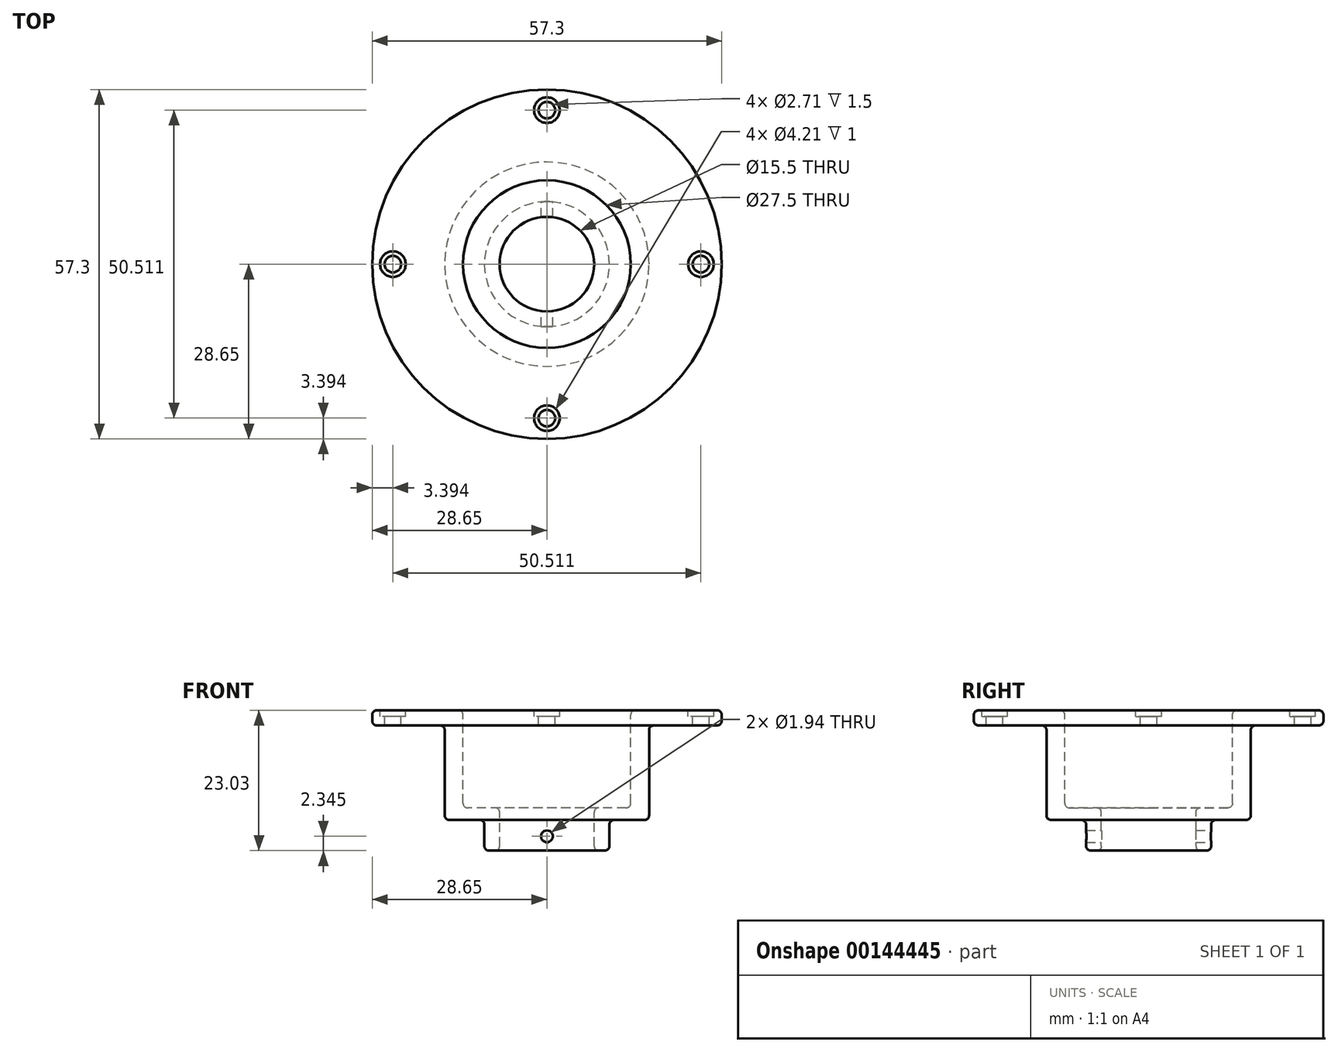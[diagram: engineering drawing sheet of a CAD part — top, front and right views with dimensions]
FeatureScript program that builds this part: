
annotation { "Feature Type Name" : "Feature", "Feature Type Description" : "" }
export const myFeature = defineFeature(function(context is Context, id is Id, definition is map)
    precondition{}
    {
        {
            var Q0;
            Q0=qCreatedBy(makeId("Front.planeOp"),FACE);
            var sketch = newSketch(context, id + "F0", { "sketchPlane" : qUnion([Q0])});
            skLineSegment(sketch, "E0", {"start": v(0, 0) * mm, "end": v(7.75, 0) * mm});
            skLineSegment(sketch, "E1", {"start": v(7.75, 0) * mm, "end": v(7.75, 7.03) * mm});
            skLineSegment(sketch, "E2", {"start": v(7.75, 7.03) * mm, "end": v(13.75, 7.03) * mm});
            skLineSegment(sketch, "E3", {"start": v(13.75, 7.03) * mm, "end": v(13.75, 23.03) * mm});
            skLineSegment(sketch, "E4", {"start": v(13.75, 23.03) * mm, "end": v(28.65, 23.03) * mm});
            skLineSegment(sketch, "E5", {"start": v(28.65, 23.03) * mm, "end": v(28.65, 20.53) * mm});
            skLineSegment(sketch, "E6", {"start": v(28.65, 20.53) * mm, "end": v(16.75, 20.53) * mm});
            skLineSegment(sketch, "E7", {"start": v(16.75, 20.53) * mm, "end": v(16.75, 5.03) * mm});
            skLineSegment(sketch, "E8", {"start": v(16.75, 5.03) * mm, "end": v(10.25, 5.03) * mm});
            skLineSegment(sketch, "E9", {"start": v(10.25, 5.03) * mm, "end": v(10.25, 0) * mm});
            skLineSegment(sketch, "E10", {"start": v(10.25, 0) * mm, "end": v(7.75, 0) * mm});
            skLineSegment(sketch, "E11", {"start": v(0, 26.24) * mm, "end": v(0, -4.42) * mm});
            skSolve(sketch);
        }
        {
            var Q0;
            Q0 = qSketchRegion(id + "F0", true);
            var Q1;
            Q1=sQuery(id+"F0.wireOp",EDGE,"E11");
            revolve(context, id + "F1", {"entities" : qUnion([Q0]), "axis" : qUnion([Q1]), "revolveType" : RevolveType.FULL});
        }
        {
            var Q0;
            Q0=makeQuery(id+"F1.opRevolve","SWEPT_FACE",FACE,{"disambiguationData":[OSD([sQuery(id+"F0.wireOp",EDGE,"E4")])]});
            var sketch = newSketch(context, id + "F2", { "sketchPlane" : qUnion([Q0])});
            skCircle(sketch, "E12", {"center": v(0, 0) * mm, "radius": 25.26 * mm});
            skCircle(sketch, "E13", {"center": v(25.26, 0) * mm, "radius": 1.35 * mm});
            skCircle(sketch, "E14", {"center": v(0, 0) * mm, "radius": 26.6 * mm});
            skCircle(sketch, "E15", {"center": v(0, 25.26) * mm, "radius": 1.35 * mm});
            skCircle(sketch, "E16", {"center": v(-25.26, 0) * mm, "radius": 1.35 * mm});
            skCircle(sketch, "E17", {"center": v(0, -25.26) * mm, "radius": 1.35 * mm});
            skSolve(sketch);
        }
        {
            var Q0;
            {var subQ0=sQuery(id+"F2.wireOp",EDGE,"E17");var subQ1=sQuery(id+"F2.wireOp",EDGE,"E12");var subQ2=makeQuery(id+"F2.imprint","INTERSECT",VERTEX,{"disambiguationData":[OD(0.0)],"derivedFrom":[subQ1,subQ0]});Q0=makeQuery(id+"F2.imprint","IMPRINT",FACE,{"disambiguationData":[TD([[makeQuery(id+"F2.imprint","IMPRINT",EDGE,{"disambiguationData":[TD([[subQ2,-1.0]])],"derivedFrom":subQ1}),-1.0]])]});}
            var Q1;
            {var subQ0=sQuery(id+"F2.wireOp",EDGE,"E17");var subQ1=sQuery(id+"F2.wireOp",EDGE,"E12");var subQ2=makeQuery(id+"F2.imprint","INTERSECT",VERTEX,{"disambiguationData":[OD(0.0)],"derivedFrom":[subQ1,subQ0]});Q1=makeQuery(id+"F2.imprint","IMPRINT",FACE,{"disambiguationData":[TD([[makeQuery(id+"F2.imprint","IMPRINT",EDGE,{"disambiguationData":[TD([[subQ2,-1.0]])],"derivedFrom":subQ1}),1.0]])]});}
            var Q2;
            {var subQ0=sQuery(id+"F2.wireOp",EDGE,"E13");var subQ1=sQuery(id+"F2.wireOp",EDGE,"E12");var subQ2=makeQuery(id+"F2.imprint","INTERSECT",VERTEX,{"disambiguationData":[OD(0.0)],"derivedFrom":[subQ1,subQ0]});Q2=makeQuery(id+"F2.imprint","IMPRINT",FACE,{"disambiguationData":[TD([[makeQuery(id+"F2.imprint","IMPRINT",EDGE,{"disambiguationData":[TD([[subQ2,1.0]])],"derivedFrom":subQ1}),-1.0]])]});}
            var Q3;
            {var subQ0=sQuery(id+"F2.wireOp",EDGE,"E13");var subQ1=sQuery(id+"F2.wireOp",EDGE,"E12");var subQ2=makeQuery(id+"F2.imprint","INTERSECT",VERTEX,{"disambiguationData":[OD(0.0)],"derivedFrom":[subQ1,subQ0]});Q3=makeQuery(id+"F2.imprint","IMPRINT",FACE,{"disambiguationData":[TD([[makeQuery(id+"F2.imprint","IMPRINT",EDGE,{"disambiguationData":[TD([[subQ2,1.0]])],"derivedFrom":subQ1}),1.0]])]});}
            var Q4;
            {var subQ0=sQuery(id+"F2.wireOp",EDGE,"E15");var subQ1=sQuery(id+"F2.wireOp",EDGE,"E12");var subQ2=makeQuery(id+"F2.imprint","INTERSECT",VERTEX,{"disambiguationData":[OD(0.0)],"derivedFrom":[subQ1,subQ0]});Q4=makeQuery(id+"F2.imprint","IMPRINT",FACE,{"disambiguationData":[TD([[makeQuery(id+"F2.imprint","IMPRINT",EDGE,{"disambiguationData":[TD([[subQ2,-1.0]])],"derivedFrom":subQ1}),-1.0]])]});}
            var Q5;
            {var subQ0=sQuery(id+"F2.wireOp",EDGE,"E15");var subQ1=sQuery(id+"F2.wireOp",EDGE,"E12");var subQ2=makeQuery(id+"F2.imprint","INTERSECT",VERTEX,{"disambiguationData":[OD(0.0)],"derivedFrom":[subQ1,subQ0]});Q5=makeQuery(id+"F2.imprint","IMPRINT",FACE,{"disambiguationData":[TD([[makeQuery(id+"F2.imprint","IMPRINT",EDGE,{"disambiguationData":[TD([[subQ2,-1.0]])],"derivedFrom":subQ1}),1.0]])]});}
            var Q6;
            {var subQ0=sQuery(id+"F2.wireOp",EDGE,"E16");var subQ1=sQuery(id+"F2.wireOp",EDGE,"E12");var subQ2=makeQuery(id+"F2.imprint","INTERSECT",VERTEX,{"disambiguationData":[OD(0.0)],"derivedFrom":[subQ1,subQ0]});Q6=makeQuery(id+"F2.imprint","IMPRINT",FACE,{"disambiguationData":[TD([[makeQuery(id+"F2.imprint","IMPRINT",EDGE,{"disambiguationData":[TD([[subQ2,-1.0]])],"derivedFrom":subQ1}),-1.0]])]});}
            var Q7;
            {var subQ0=sQuery(id+"F2.wireOp",EDGE,"E16");var subQ1=sQuery(id+"F2.wireOp",EDGE,"E12");var subQ2=makeQuery(id+"F2.imprint","INTERSECT",VERTEX,{"disambiguationData":[OD(0.0)],"derivedFrom":[subQ1,subQ0]});Q7=makeQuery(id+"F2.imprint","IMPRINT",FACE,{"disambiguationData":[TD([[makeQuery(id+"F2.imprint","IMPRINT",EDGE,{"disambiguationData":[TD([[subQ2,-1.0]])],"derivedFrom":subQ1}),1.0]])]});}
            extrude(context, id + "F3", {"entities" : qUnion([Q0, Q1, Q2, Q3, Q4, Q5, Q6, Q7]), "operationType" : NewBodyOperationType.REMOVE, "oppositeDirection" : true, "depth" : 25 * mm});
        }
        {
            var Q0;
            Q0=makeQuery(id+"F1.opRevolve","SWEPT_FACE",FACE,{"disambiguationData":[OSD([sQuery(id+"F0.wireOp",EDGE,"E4")])]});
            var sketch = newSketch(context, id + "F4", { "sketchPlane" : qUnion([Q0])});
            skCircle(sketch, "E18", {"center": v(0, 0) * mm, "radius": 23.15 * mm});
            skCircle(sketch, "E19", {"center": v(25.26, 0) * mm, "radius": 2.1 * mm});
            skCircle(sketch, "E20", {"center": v(0, -25.26) * mm, "radius": 2.1 * mm});
            skCircle(sketch, "E21", {"center": v(-25.26, 0) * mm, "radius": 2.1 * mm});
            skCircle(sketch, "E22", {"center": v(0, 25.26) * mm, "radius": 2.1 * mm});
            skSolve(sketch);
        }
        {
            var Q0;
            Q0=makeQuery(id+"F4.imprint","IMPRINT",FACE,{"disambiguationData":[TD([[makeQuery(id+"F4.imprint","IMPRINT",EDGE,{"derivedFrom":sQuery(id+"F4.wireOp",EDGE,"E20")}),1.0]])]});
            var Q1;
            Q1=makeQuery(id+"F4.imprint","IMPRINT",FACE,{"disambiguationData":[TD([[makeQuery(id+"F4.imprint","IMPRINT",EDGE,{"derivedFrom":sQuery(id+"F4.wireOp",EDGE,"E21")}),1.0]])]});
            var Q2;
            Q2=makeQuery(id+"F4.imprint","IMPRINT",FACE,{"disambiguationData":[TD([[makeQuery(id+"F4.imprint","IMPRINT",EDGE,{"derivedFrom":sQuery(id+"F4.wireOp",EDGE,"E22")}),1.0]])]});
            var Q3;
            Q3=makeQuery(id+"F4.imprint","IMPRINT",FACE,{"disambiguationData":[TD([[makeQuery(id+"F4.imprint","IMPRINT",EDGE,{"derivedFrom":sQuery(id+"F4.wireOp",EDGE,"E19")}),1.0]])]});
            extrude(context, id + "F5", {"entities" : qUnion([Q0, Q1, Q2, Q3]), "operationType" : NewBodyOperationType.REMOVE, "oppositeDirection" : true, "depth" : 1 * mm});
        }
        {
            var Q0;
            Q0=makeQuery(id+"F1.opRevolve","SWEPT_EDGE",EDGE,{"disambiguationData":[OSD([sQuery(id+"F0.wireOp",EDGE,"E3"),sQuery(id+"F0.wireOp",EDGE,"E4")])]});
            var Q1;
            Q1=makeQuery(id+"F1.opRevolve","SWEPT_EDGE",EDGE,{"disambiguationData":[OSD([sQuery(id+"F0.wireOp",EDGE,"E4"),sQuery(id+"F0.wireOp",EDGE,"E5")])]});
            var Q2;
            Q2=makeQuery(id+"F1.opRevolve","SWEPT_EDGE",EDGE,{"disambiguationData":[OSD([sQuery(id+"F0.wireOp",EDGE,"E5"),sQuery(id+"F0.wireOp",EDGE,"E6")])]});
            var Q3;
            Q3=makeQuery(id+"F1.opRevolve","SWEPT_EDGE",EDGE,{"disambiguationData":[OSD([sQuery(id+"F0.wireOp",EDGE,"E6"),sQuery(id+"F0.wireOp",EDGE,"E7")])]});
            var Q4;
            Q4=makeQuery(id+"F1.opRevolve","SWEPT_EDGE",EDGE,{"disambiguationData":[OSD([sQuery(id+"F0.wireOp",EDGE,"E7"),sQuery(id+"F0.wireOp",EDGE,"E8")])]});
            var Q5;
            Q5=makeQuery(id+"F1.opRevolve","SWEPT_EDGE",EDGE,{"disambiguationData":[OSD([sQuery(id+"F0.wireOp",EDGE,"E8"),sQuery(id+"F0.wireOp",EDGE,"E9")])]});
            var Q6;
            Q6=makeQuery(id+"F1.opRevolve","SWEPT_EDGE",EDGE,{"disambiguationData":[OSD([sQuery(id+"F0.wireOp",EDGE,"E9"),sQuery(id+"F0.wireOp",EDGE,"E10")])]});
            var Q7;
            Q7=makeQuery(id+"F1.opRevolve","SWEPT_EDGE",EDGE,{"disambiguationData":[OSD([sQuery(id+"F0.wireOp",EDGE,"E1"),sQuery(id+"F0.wireOp",EDGE,"E10")])]});
            var Q8;
            Q8=makeQuery(id+"F1.opRevolve","SWEPT_EDGE",EDGE,{"disambiguationData":[OSD([sQuery(id+"F0.wireOp",EDGE,"E1"),sQuery(id+"F0.wireOp",EDGE,"E2")])]});
            var Q9;
            Q9=makeQuery(id+"F1.opRevolve","SWEPT_EDGE",EDGE,{"disambiguationData":[OSD([sQuery(id+"F0.wireOp",EDGE,"E2"),sQuery(id+"F0.wireOp",EDGE,"E3")])]});
            fillet(context, id + "F6", {"entities" : qUnion([Q0, Q1, Q2, Q3, Q4, Q5, Q6, Q7, Q8, Q9]), "radius" : .750 * mm, "tangentPropagation" : true, "allowEdgeOverflow" : false});
        }
        {
            var Q0;
            Q0=qCreatedBy(makeId("Front.planeOp"),FACE);
            var sketch = newSketch(context, id + "F7", { "sketchPlane" : qUnion([Q0])});
            skCircle(sketch, "E23", {"center": v(0, 2.34) * mm, "radius": 0.97 * mm});
            skSolve(sketch);
        }
        {
            var Q0;
            Q0=makeQuery(id+"F7.imprint","IMPRINT",FACE,{"disambiguationData":[TD([[makeQuery(id+"F7.imprint","IMPRINT",EDGE,{"derivedFrom":sQuery(id+"F7.wireOp",EDGE,"E23")}),1.0]])]});
            extrude(context, id + "F8", {"entities" : qUnion([Q0]), "operationType" : NewBodyOperationType.REMOVE, "endBound" : BoundingType.SYMMETRIC, "depth" : 25.62 * mm});
        }
    });
